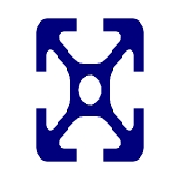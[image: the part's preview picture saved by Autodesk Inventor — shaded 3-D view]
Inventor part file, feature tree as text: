
AUTODESK INVENTOR PART (.ipt)
format: ipt  version: 2020 (Build 240168000, 168)  size: 274,432 bytes
history: native  units: mm
features: other x16, sketch x8
ambient origin geometry x8: Origin, YZ Plane, XZ Plane, XY Plane, X Axis, Y Axis, Z Axis, Center Point
bodies: Body (feature_tree)
feature tree (24):
  other  "Řízená délka"
  other  "Těleso1"
  other  "Start Plane"
  other  "End Plane"
  other  "iFeatureSketch"
  other  "DRAZKA_20:1"
  other  "DRAZKA_20:2"
  other  "DRAZKA_20:3"
  other  "DRAZKA_20:4"
  other  "DIRA_20:1"
  other  "DRAZKA_20:1Axis"
  other  "DRAZKA_20:2Axis"
  other  "DRAZKA_20:3Axis"
  other  "DRAZKA_20:4Axis"
  other  "DIRA_20:1Axis"
  sketch  "Sketch"  dims[d2=20.0mm d3=20.0mm d4=2.0mm d9=-0.0mm d10=480.952381mm d11=0.13mm d12=0.0mm d15=0.83mm d16=0.83mm d17=9.8mm d18=3.0mm d19=4.55mm d20=45.0deg d21=5.2mm d22=1.8mm d24=1.0mm d26=0.83mm d27=0.83mm d28=9.8mm d29=3.0mm d30=4.55mm d31=45.0deg d32=5.2mm d33=1.8mm d35=1.0mm d37=0.83mm d38=0.83mm d39=9.8mm d40=3.0mm d41=4.55mm d42=45.0deg d43=5.2mm d44=1.8mm d46=1.0mm d48=0.83mm d49=0.83mm d50=9.8mm d51=3.0mm d52=4.55mm d53=45.0deg d54=5.2mm d55=1.8mm d57=1.0mm d59=4.3mm d60=0.0mm d61=0.0mm d62=0.0mm d63=0.0mm d64=0.0mm d65=0.0mm d66=0.0mm d67=0.0mm d76=90.0deg d14=480.952381mm]
  sketch  "Náčrt11"
  other  "Pracovní rovina4"
  sketch  "Náčrt12"
  sketch  "Náčrt6"
  sketch  "Náčrt7"
  sketch  "Náčrt8"
  sketch  "Náčrt9"
  sketch  "Náčrt10"
